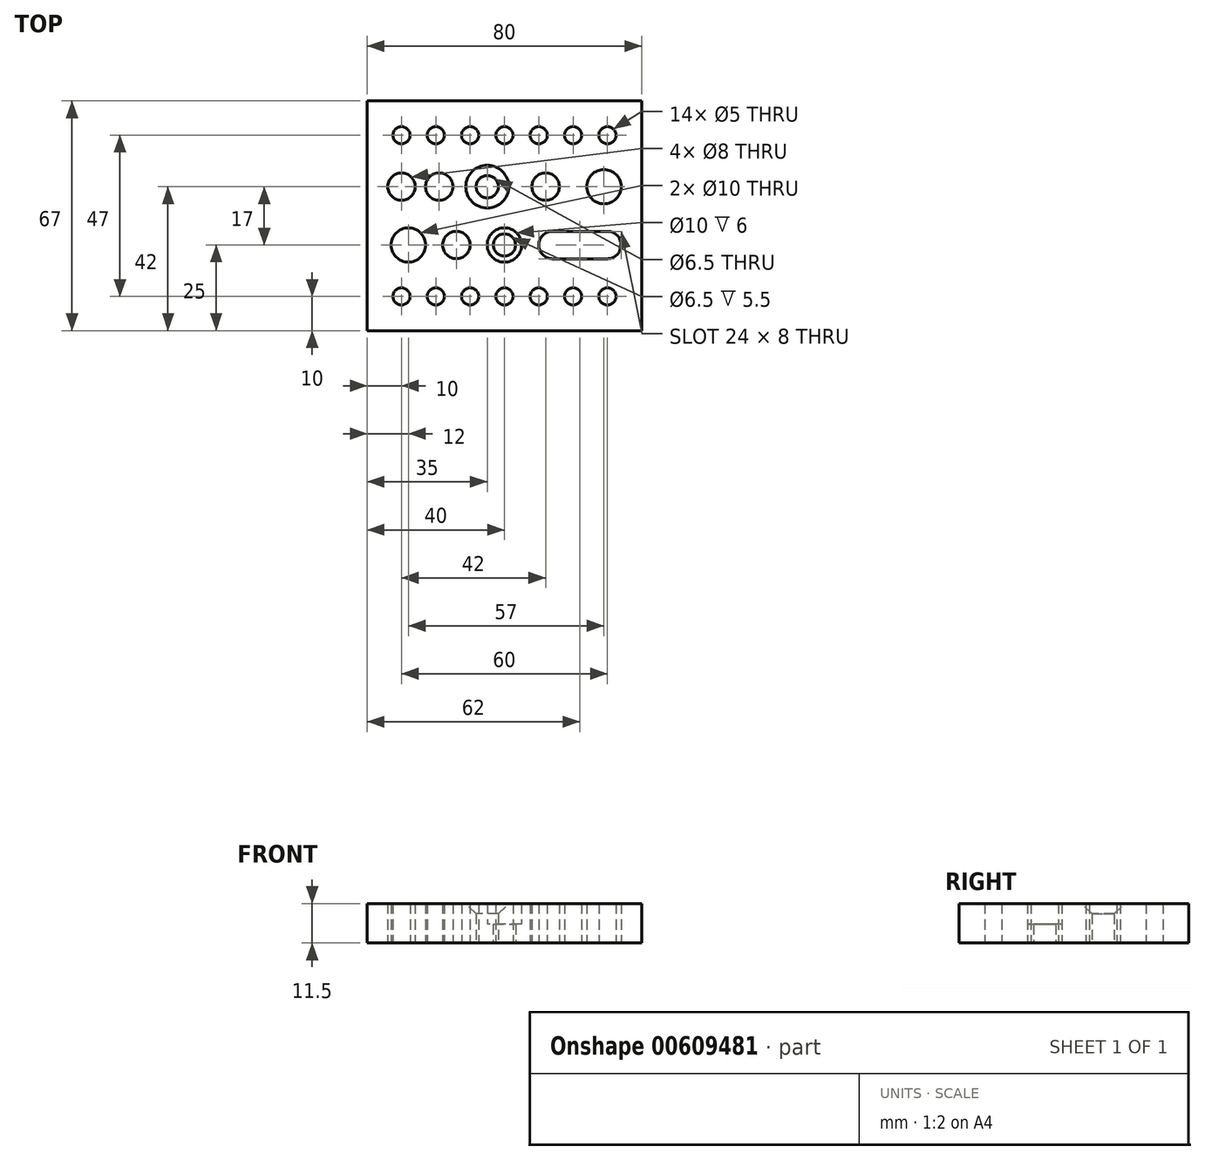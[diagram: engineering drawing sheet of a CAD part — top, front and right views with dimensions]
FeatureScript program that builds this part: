
annotation { "Feature Type Name" : "Feature", "Feature Type Description" : "" }
export const myFeature = defineFeature(function(context is Context, id is Id, definition is map)
    precondition{}
    {
        {
            var Q0;
            Q0=qCreatedBy(makeId("Top.planeOp"),FACE);
            var sketch = newSketch(context, id + "F0", { "sketchPlane" : qUnion([Q0])});
            skLineSegment(sketch, "E0.bottom", {"start": v(0, 0) * mm, "end": v(80, 0) * mm});
            skLineSegment(sketch, "E0.top", {"start": v(0, 67) * mm, "end": v(80, 67) * mm});
            skLineSegment(sketch, "E0.left", {"start": v(0, 0) * mm, "end": v(0, 67) * mm});
            skLineSegment(sketch, "E0.right", {"start": v(80, 0) * mm, "end": v(80, 67) * mm});
            skCircle(sketch, "E1", {"center": v(10, 10) * mm, "radius": 2.5 * mm});
            skCircle(sketch, "E2", {"center": v(10, 57) * mm, "radius": 2.5 * mm});
            skCircle(sketch, "E3.1.0.0", {"center": v(20, 57) * mm, "radius": 2.5 * mm});
            skCircle(sketch, "E3.1.0.1", {"center": v(20, 10) * mm, "radius": 2.5 * mm});
            skCircle(sketch, "E3.2.0.0", {"center": v(30, 57) * mm, "radius": 2.5 * mm});
            skCircle(sketch, "E3.2.0.1", {"center": v(30, 10) * mm, "radius": 2.5 * mm});
            skCircle(sketch, "E3.3.0.0", {"center": v(40, 57) * mm, "radius": 2.5 * mm});
            skCircle(sketch, "E3.3.0.1", {"center": v(40, 10) * mm, "radius": 2.5 * mm});
            skCircle(sketch, "E3.4.0.0", {"center": v(50, 57) * mm, "radius": 2.5 * mm});
            skCircle(sketch, "E3.4.0.1", {"center": v(50, 10) * mm, "radius": 2.5 * mm});
            skCircle(sketch, "E3.5.0.0", {"center": v(60, 57) * mm, "radius": 2.5 * mm});
            skCircle(sketch, "E3.5.0.1", {"center": v(60, 10) * mm, "radius": 2.5 * mm});
            skCircle(sketch, "E3.6.0.0", {"center": v(70, 57) * mm, "radius": 2.5 * mm});
            skCircle(sketch, "E3.6.0.1", {"center": v(70, 10) * mm, "radius": 2.5 * mm});
            skLineSegment(sketch, "E3.direction1", {"start": v(10, 57) * mm, "end": v(20, 57) * mm, "construction": true});
            skLineSegment(sketch, "E4", {"start": v(70, 25) * mm, "end": v(54, 25) * mm, "construction": true});
            skCircle(sketch, "E5", {"center": v(12, 25) * mm, "radius": 5 * mm});
            skCircle(sketch, "E6", {"center": v(26, 25) * mm, "radius": 4 * mm});
            skCircle(sketch, "E7", {"center": v(40, 25) * mm, "radius": 5 * mm});
            skArc(sketch, "E8.0.startCap", {"start": v(70, 29) * mm, "mid": v(74, 25) * mm, "end": v(70, 21) * mm});
            skArc(sketch, "E8.0.endCap", {"start": v(54, 21) * mm, "mid": v(50, 25) * mm, "end": v(54, 29) * mm});
            skLineSegment(sketch, "E8.0.left", {"start": v(70, 21) * mm, "end": v(54, 21) * mm});
            skLineSegment(sketch, "E8.0.right", {"start": v(70, 29) * mm, "end": v(54, 29) * mm});
            skCircle(sketch, "E9", {"center": v(69, 42) * mm, "radius": 5 * mm});
            skCircle(sketch, "E10", {"center": v(52, 42) * mm, "radius": 4 * mm});
            skCircle(sketch, "E11", {"center": v(35, 42) * mm, "radius": 3.25 * mm});
            skCircle(sketch, "E12", {"center": v(21, 42) * mm, "radius": 4 * mm});
            skCircle(sketch, "E13", {"center": v(10, 42) * mm, "radius": 4 * mm});
            skSolve(sketch);
        }
        {
            var Q0;
            Q0=makeQuery(id+"F0.imprint","IMPRINT",FACE,{"disambiguationData":[TD([[makeQuery(id+"F0.imprint","IMPRINT",EDGE,{"derivedFrom":sQuery(id+"F0.wireOp",EDGE,"E0.bottom")}),1.0]])]});
            extrude(context, id + "F1", {"entities" : qUnion([Q0]), "depth" : 11.5 * mm, "offsetDistance" : 25 * mm});
        }
        {
            var Q0;
            Q0=makeQuery(id+"F1.opExtrude","CAP_EDGE",EDGE,{"disambiguationData":[OSD([sQuery(id+"F0.wireOp",EDGE,"E11")])],"isStart":false});
            chamfer(context, id + "F2", {"entities" : qUnion([Q0]), "chamferType" : ChamferType.OFFSET_ANGLE, "width" : 3 * mm, "oppositeDirection" : false, "angle" : 45 * degree, "tangentPropagation" : true});
        }
        {
            var Q0;
            Q0=makeQuery(id+"F1.opExtrude","CAP_FACE",FACE,{"disambiguationData":[OSD([sQuery(id+"F0.wireOp",EDGE,"E0.bottom"),sQuery(id+"F0.wireOp",EDGE,"E0.top"),sQuery(id+"F0.wireOp",EDGE,"E0.left"),sQuery(id+"F0.wireOp",EDGE,"E0.right"),sQuery(id+"F0.wireOp",EDGE,"E1"),sQuery(id+"F0.wireOp",EDGE,"E2"),sQuery(id+"F0.wireOp",EDGE,"E3.1.0.0"),sQuery(id+"F0.wireOp",EDGE,"E3.1.0.1"),sQuery(id+"F0.wireOp",EDGE,"E3.2.0.0"),sQuery(id+"F0.wireOp",EDGE,"E3.2.0.1"),sQuery(id+"F0.wireOp",EDGE,"E3.3.0.0"),sQuery(id+"F0.wireOp",EDGE,"E3.3.0.1"),sQuery(id+"F0.wireOp",EDGE,"E3.4.0.0"),sQuery(id+"F0.wireOp",EDGE,"E3.4.0.1"),sQuery(id+"F0.wireOp",EDGE,"E3.5.0.0"),sQuery(id+"F0.wireOp",EDGE,"E3.5.0.1"),sQuery(id+"F0.wireOp",EDGE,"E3.6.0.0"),sQuery(id+"F0.wireOp",EDGE,"E3.6.0.1"),sQuery(id+"F0.wireOp",EDGE,"E5"),sQuery(id+"F0.wireOp",EDGE,"E6"),sQuery(id+"F0.wireOp",EDGE,"E7"),sQuery(id+"F0.wireOp",EDGE,"E8.0.startCap"),sQuery(id+"F0.wireOp",EDGE,"E8.0.endCap"),sQuery(id+"F0.wireOp",EDGE,"E8.0.left"),sQuery(id+"F0.wireOp",EDGE,"E8.0.right"),sQuery(id+"F0.wireOp",EDGE,"E9"),sQuery(id+"F0.wireOp",EDGE,"E10"),sQuery(id+"F0.wireOp",EDGE,"E11"),sQuery(id+"F0.wireOp",EDGE,"E12"),sQuery(id+"F0.wireOp",EDGE,"E13")])],"isStart":true});
            var sketch = newSketch(context, id + "F3", { "sketchPlane" : qUnion([Q0])});
            skCircle(sketch, "E14", {"center": v(40, -25) * mm, "radius": 3.25 * mm});
            skCircle(sketch, "E15", {"center": v(40, -25) * mm, "radius": 5 * mm});
            skSolve(sketch);
        }
        {
            var Q0;
            Q0=makeQuery(id+"F3.imprint","IMPRINT",FACE,{"disambiguationData":[TD([[makeQuery(id+"F3.imprint","IMPRINT",EDGE,{"derivedFrom":sQuery(id+"F3.wireOp",EDGE,"E14")}),-1.0]])]});
            extrude(context, id + "F4", {"entities" : qUnion([Q0]), "operationType" : NewBodyOperationType.ADD, "oppositeDirection" : true, "depth" : (11.5 - 6) * mm, "offsetDistance" : 25 * mm});
        }
    });
